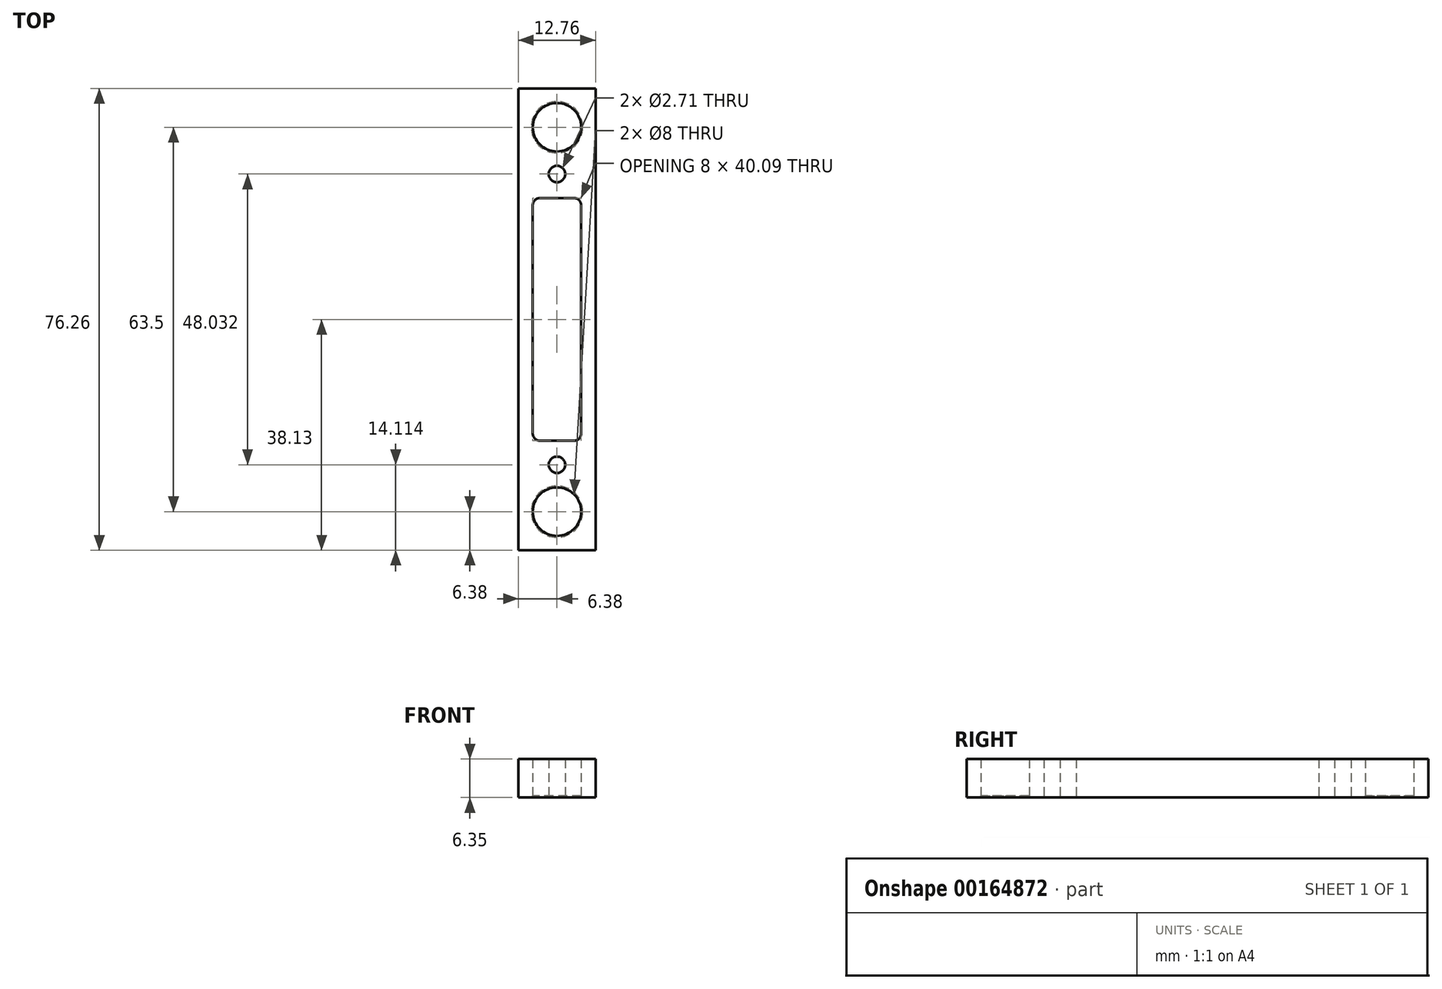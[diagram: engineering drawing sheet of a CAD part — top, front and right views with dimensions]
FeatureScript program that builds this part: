
annotation { "Feature Type Name" : "Feature", "Feature Type Description" : "" }
export const myFeature = defineFeature(function(context is Context, id is Id, definition is map)
    precondition{}
    {
        {
            var Q0;
            Q0=qCreatedBy(makeId("Top.planeOp"),FACE);
            var sketch = newSketch(context, id + "F0", { "sketchPlane" : qUnion([Q0])});
            skLineSegment(sketch, "E0.bottom", {"start": v(4, 20.05) * mm, "end": v(-4, 20.05) * mm});
            skLineSegment(sketch, "E0.top", {"start": v(4, -20.05) * mm, "end": v(-4, -20.05) * mm});
            skLineSegment(sketch, "E0.left", {"start": v(4, 20.05) * mm, "end": v(4, -20.05) * mm});
            skLineSegment(sketch, "E0.right", {"start": v(-4, 20.05) * mm, "end": v(-4, -20.05) * mm});
            skPoint(sketch, "E0.middle", {"position": v(0, 0) * mm});
            skLineSegment(sketch, "E1.bottom", {"start": v(6.38, 38.13) * mm, "end": v(-6.38, 38.13) * mm});
            skLineSegment(sketch, "E1.top", {"start": v(6.38, -38.13) * mm, "end": v(-6.38, -38.13) * mm});
            skLineSegment(sketch, "E1.left", {"start": v(6.38, 38.13) * mm, "end": v(6.38, -38.13) * mm});
            skLineSegment(sketch, "E1.right", {"start": v(-6.38, 38.13) * mm, "end": v(-6.38, -38.13) * mm});
            skLineSegment(sketch, "E2", {"start": v(0, 20.05) * mm, "end": v(0, 24.02) * mm, "construction": true});
            skLineSegment(sketch, "E3", {"start": v(0, 24.02) * mm, "end": v(0, 31.75) * mm, "construction": true});
            skLineSegment(sketch, "E4", {"start": v(4, 0) * mm, "end": v(6.38, 0) * mm, "construction": true});
            skLineSegment(sketch, "E5", {"start": v(0, -20.05) * mm, "end": v(0, -24.02) * mm, "construction": true});
            skLineSegment(sketch, "E6", {"start": v(0, -24.02) * mm, "end": v(0, -31.75) * mm, "construction": true});
            skCircle(sketch, "E7", {"center": v(0, 24.02) * mm, "radius": 1.35 * mm});
            skCircle(sketch, "E8", {"center": v(0, 31.75) * mm, "radius": 4 * mm});
            skCircle(sketch, "E9", {"center": v(0, -31.75) * mm, "radius": 4 * mm});
            skCircle(sketch, "E10", {"center": v(0, -24.02) * mm, "radius": 1.35 * mm});
            skSolve(sketch);
        }
        {
            var Q0;
            Q0 = qSketchRegion(id + "F0", true);
            extrude(context, id + "F1", {"entities" : qUnion([Q0]), "depth" : 6.35 * mm});
        }
        {
            var Q0;
            Q0=makeQuery(id+"F1.opExtrude","SWEPT_EDGE",EDGE,{"disambiguationData":[OSD([sQuery(id+"F0.wireOp",EDGE,"E0.bottom"),sQuery(id+"F0.wireOp",EDGE,"E0.right")])]});
            var Q1;
            Q1=makeQuery(id+"F1.opExtrude","SWEPT_EDGE",EDGE,{"disambiguationData":[OSD([sQuery(id+"F0.wireOp",EDGE,"E0.bottom"),sQuery(id+"F0.wireOp",EDGE,"E0.left")])]});
            var Q2;
            Q2=makeQuery(id+"F1.opExtrude","SWEPT_EDGE",EDGE,{"disambiguationData":[OSD([sQuery(id+"F0.wireOp",EDGE,"E0.top"),sQuery(id+"F0.wireOp",EDGE,"E0.left")])]});
            var Q3;
            Q3=makeQuery(id+"F1.opExtrude","SWEPT_EDGE",EDGE,{"disambiguationData":[OSD([sQuery(id+"F0.wireOp",EDGE,"E0.top"),sQuery(id+"F0.wireOp",EDGE,"E0.right")])]});
            fillet(context, id + "F2", {"entities" : qUnion([Q0, Q1, Q2, Q3]), "radius" : 1.2 * mm, "tangentPropagation" : true, "allowEdgeOverflow" : false});
        }
        {
            var Q0;
            Q0=makeQuery(id+"F1.opExtrude","CAP_EDGE",EDGE,{"disambiguationData":[OSD([sQuery(id+"F0.wireOp",EDGE,"E8")])],"isStart":true});
            var Q1;
            Q1=makeQuery(id+"F1.opExtrude","CAP_EDGE",EDGE,{"disambiguationData":[OSD([sQuery(id+"F0.wireOp",EDGE,"E9")])],"isStart":true});
            chamfer(context, id + "F3", {"entities" : qUnion([Q0, Q1]), "width" : 0.25 * mm, "tangentPropagation" : true});
        }
    });
